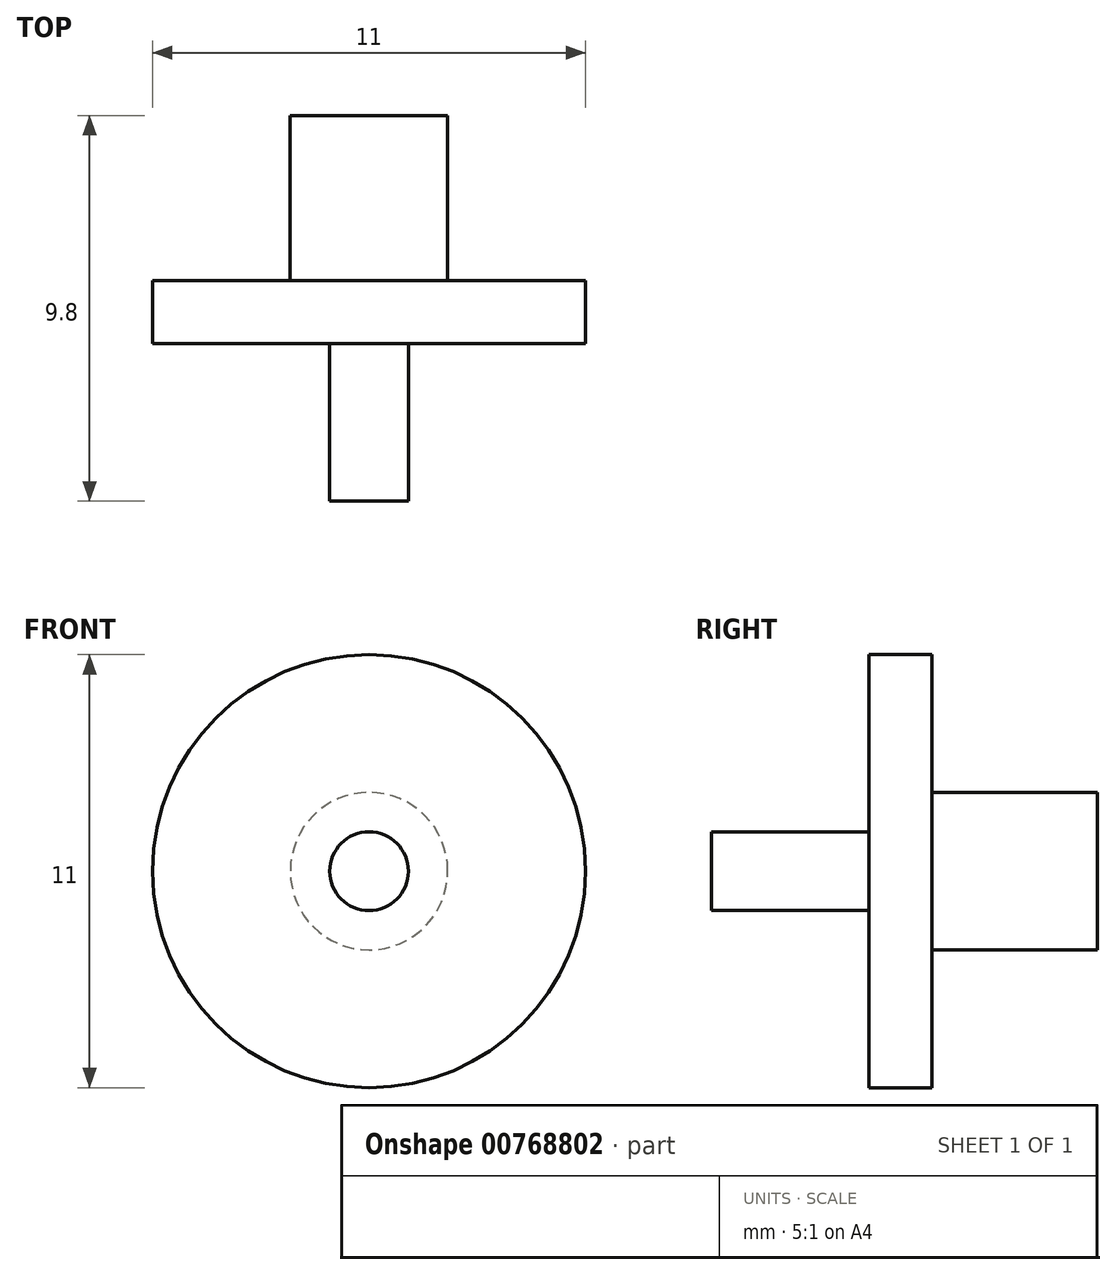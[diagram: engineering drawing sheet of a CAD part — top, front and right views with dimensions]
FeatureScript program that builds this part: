
annotation { "Feature Type Name" : "Feature", "Feature Type Description" : "" }
export const myFeature = defineFeature(function(context is Context, id is Id, definition is map)
    precondition{}
    {
        {
            var Q0;
            Q0=qCreatedBy(makeId("Right.planeOp"),FACE);
            var sketch = newSketch(context, id + "F0", { "sketchPlane" : qUnion([Q0])});
            skLineSegment(sketch, "E0.top", {"start": v(-1.4, 5.5) * mm, "end": v(-3, 5.5) * mm});
            skPoint(sketch, "E0.middle", {"position": v(0, 0) * mm});
            skLineSegment(sketch, "E1.top", {"start": v(-7, 1) * mm, "end": v(-3, 1) * mm});
            skLineSegment(sketch, "E1.left", {"start": v(-7, 0) * mm, "end": v(-7, 1) * mm});
            skLineSegment(sketch, "E2.top", {"start": v(2.8, 2) * mm, "end": v(-1.4, 2) * mm});
            skLineSegment(sketch, "E2.left", {"start": v(2.8, 0) * mm, "end": v(2.8, 2) * mm});
            skLineSegment(sketch, "E3", {"start": v(-1.4, 2) * mm, "end": v(-1.4, 5.5) * mm});
            skLineSegment(sketch, "E4.trimOffspring", {"start": v(-3, 1) * mm, "end": v(-3, 5.5) * mm});
            skLineSegment(sketch, "E5", {"start": v(-7, 0) * mm, "end": v(2.8, 0) * mm});
            skSolve(sketch);
        }
        {
            var Q0;
            Q0=makeQuery(id+"F0.imprint","IMPRINT",FACE,{"disambiguationData":[TD([[makeQuery(id+"F0.imprint","IMPRINT",EDGE,{"derivedFrom":sQuery(id+"F0.wireOp",EDGE,"E0.top")}),1.0]])]});
            var Q1;
            Q1=sQuery(id+"F0.wireOp",EDGE,"E5");
            revolve(context, id + "F1", {"surfaceOperationType" : NewSurfaceOperationType.NEW, "entities" : qUnion([Q0]), "axis" : qUnion([Q1]), "revolveType" : RevolveType.FULL});
        }
    });
